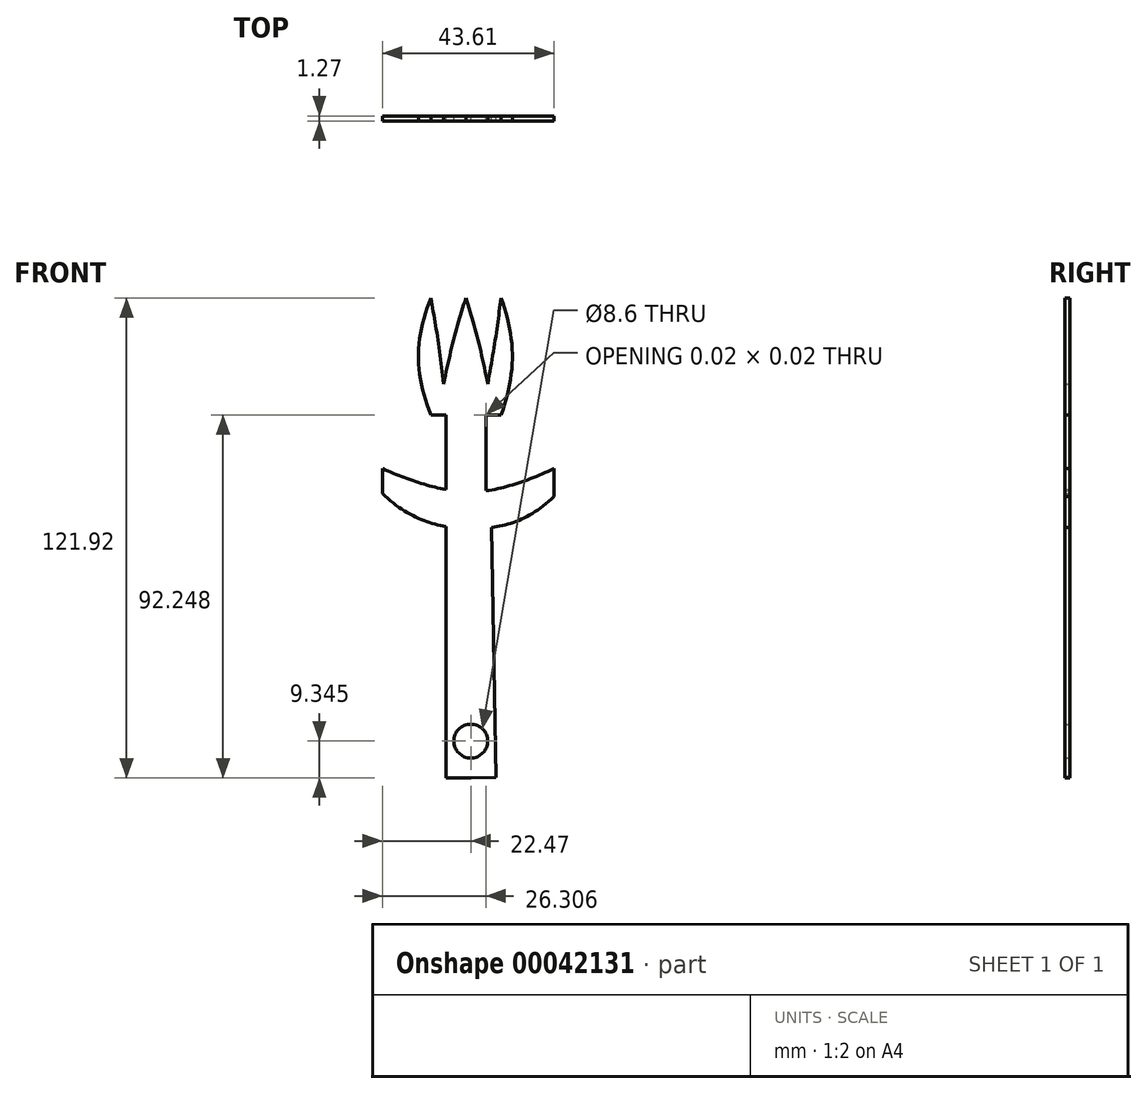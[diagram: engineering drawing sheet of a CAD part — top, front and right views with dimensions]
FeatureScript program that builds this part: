
annotation { "Feature Type Name" : "Feature", "Feature Type Description" : "" }
export const myFeature = defineFeature(function(context is Context, id is Id, definition is map)
    precondition{}
    {
        {
            var Q0;
            Q0=qCreatedBy(makeId("Front.planeOp"),FACE);
            var sketch = newSketch(context, id + "F0", { "sketchPlane" : qUnion([Q0])});
            skLineSegment(sketch, "E0", {"start": v(0, 0) * mm, "end": v(-6.35, 0) * mm});
            skLineSegment(sketch, "E1", {"start": v(0, 0) * mm, "end": v(6.35, 0.1) * mm});
            skFitSpline(sketch, "E2", {"points": [v(-22.47, 72.22) * mm, v(0, 63.3) * mm, v(21.14, 71.52) * mm], "startDerivative": vector(44.65, -42.56) * mm, "endDerivative": vector(42.56, 41.57) * mm});
            skLineSegment(sketch, "E3", {"start": v(-22.47, 72.22) * mm, "end": v(-22.47, 78.57) * mm});
            skLineSegment(sketch, "E4", {"start": v(21.14, 71.52) * mm, "end": v(21.14, 78.57) * mm});
            skFitSpline(sketch, "E5", {"points": [v(-22.47, 78.57) * mm, v(0, 72.7) * mm, v(21.14, 78.57) * mm], "startDerivative": vector(44.68, -19.03) * mm, "endDerivative": vector(42.53, 19.2) * mm});
            skPoint(sketch, "E6.end.orphan", {"position": v(17.01, 87.66) * mm});
            skPoint(sketch, "E7.start.orphan", {"position": v(12.12, 63.3) * mm});
            skPoint(sketch, "E8.start.orphan", {"position": v(-12.7, 63.3) * mm});
            skLineSegment(sketch, "E9", {"start": v(-6.35, 0) * mm, "end": v(-6.35, 63.83) * mm});
            skLineSegment(sketch, "E10", {"start": v(6.35, 0.1) * mm, "end": v(5.27, 63.6) * mm});
            skPoint(sketch, "E11.end.orphan", {"position": v(-6.75, 87.66) * mm});
            skLineSegment(sketch, "E12", {"start": v(-6.35, 92.26) * mm, "end": v(-6.35, 73.27) * mm});
            skPoint(sketch, "E13.orphan", {"position": v(0, 100.12) * mm});
            skPoint(sketch, "E14.orphan", {"position": v(5.27, 121.92) * mm});
            skPoint(sketch, "E15.1.internal.orphan", {"position": v(0, 137.97) * mm});
            skPoint(sketch, "E15.endDerivative.orphan", {"position": v(5.27, 97.92) * mm});
            skPoint(sketch, "E15.startDerivative.orphan", {"position": v(0, 121.92) * mm});
            skLineSegment(sketch, "E16", {"start": v(3.84, 92.26) * mm, "end": v(3.83, 92.26) * mm});
            skLineSegment(sketch, "E17", {"start": v(3.83, 92.26) * mm, "end": v(3.83, 72.96) * mm});
            skPoint(sketch, "E18.orphan", {"position": v(0, 92.26) * mm});
            skCircle(sketch, "E19", {"center": v(0, 9.34) * mm, "radius": 4.3 * mm});
            skLineSegment(sketch, "E20", {"start": v(-6.35, 92.26) * mm, "end": v(-6.38, 92.26) * mm});
            skPoint(sketch, "E21.start.orphan", {"position": v(-6.35, 121.92) * mm});
            skEllipticalArc(sketch, "E22", {});
            skPoint(sketch, "E23.orphan", {"position": v(-1.28, 121.92) * mm});
            skPoint(sketch, "E24.start.orphan", {"position": v(-1.26, 92.26) * mm});
            skPoint(sketch, "E25.orphan", {"position": v(7.65, 92.26) * mm});
            skLineSegment(sketch, "E26", {"start": v(-6.35, 92.22) * mm, "end": v(3.84, 92.22) * mm});
            skEllipticalArc(sketch, "E27.trimOffspring", {});
            skLineSegment(sketch, "E28", {"start": v(3.84, 92.22) * mm, "end": v(7.65, 92.22) * mm});
            skLineSegment(sketch, "E29", {"start": v(-6.35, 92.22) * mm, "end": v(-10.16, 92.22) * mm});
            skFitSpline(sketch, "E30", {"points": [v(-10.16, 92.22) * mm, v(-13.31, 107.1) * mm, v(-10.16, 121.92) * mm], "startDerivative": vector(-11.42, 29.74) * mm, "endDerivative": vector(11.43, 29.67) * mm});
            skPoint(sketch, "E31.1.internal.orphan", {"position": v(10.56, 107.1) * mm});
            skPoint(sketch, "E31.end.orphan", {"position": v(7.65, 121.92) * mm});
            skFitSpline(sketch, "E32", {"points": [v(7.65, 92.22) * mm, v(10.56, 107.1) * mm, v(7.65, 121.92) * mm], "startDerivative": vector(11.3, 29.74) * mm, "endDerivative": vector(-11.3, 29.67) * mm});
            skLineSegment(sketch, "E33", {"start": v(-6.9, 121.92) * mm, "end": v(-6.9, 121.92) * mm});
            skPoint(sketch, "E34.1.internal.orphan", {"position": v(-10.16, 112.43) * mm});
            skPoint(sketch, "E35.start.orphan", {"position": v(-6.9, 100.12) * mm});
            skPoint(sketch, "E36.1.internal.orphan", {"position": v(-6.9, 112.43) * mm});
            skPoint(sketch, "E37.1.internal.orphan", {"position": v(-4.08, 112.43) * mm});
            skPoint(sketch, "E38.start.orphan", {"position": v(5.27, 100.12) * mm});
            skPoint(sketch, "E39.end.orphan", {"position": v(-1.26, 121.92) * mm});
            skFitSpline(sketch, "E40", {"points": [v(-10.16, 121.92) * mm, v(-8.52, 112.43) * mm, v(-6.9, 100.12) * mm], "startDerivative": vector(3.6, -19.6) * mm, "endDerivative": vector(2.91, -23.92) * mm});
            skFitSpline(sketch, "E41", {"points": [v(-6.9, 100.12) * mm, v(-4.08, 112.43) * mm, v(-1.26, 121.92) * mm], "startDerivative": vector(5.15, 24) * mm, "endDerivative": vector(6.16, 19.51) * mm});
            skFitSpline(sketch, "E42", {"points": [v(-1.26, 121.92) * mm, v(1.57, 112.43) * mm, v(4.32, 100.12) * mm], "startDerivative": vector(6.22, -19.5) * mm, "endDerivative": vector(4.97, -24.02) * mm});
            skFitSpline(sketch, "E43", {"points": [v(7.65, 121.92) * mm, v(6.38, 112.43) * mm, v(4.32, 100.12) * mm], "startDerivative": vector(-2.45, -19.69) * mm, "endDerivative": vector(-4.18, -23.83) * mm});
            skPoint(sketch, "E44.end.orphan", {"position": v(-1.25, 92.22) * mm});
            skPoint(sketch, "E45.end.orphan", {"position": v(-12.55, 100.12) * mm});
            skPoint(sketch, "E46.start.orphan", {"position": v(-1.26, 100.12) * mm});
            skPoint(sketch, "E47.orphan", {"position": v(9.9, 100.12) * mm});
            const initialGuessF0  = {"E22": [-0.00127, 0.10709014901935063, 0, -1, 0.017645876799215893, 0.009439947865050294, 5.710609058103408, 5.714958242728358], "E27.trimOffspring": [-0.00127, 0.10709014901935063, 0, -1, 0.017645876799215893, 0.009439947865050294, 0.568227064451229, 0.572576249076178]};
            skSetInitialGuess(sketch, initialGuessF0);
            skSolve(sketch);
        }
        {
            var Q0;
            Q0=qSketchRegion(id+"F0",true);
            extrude(context, id + "F1", {"entities" : qUnion([Q0]), "depth" : 1.27 * mm});
        }
    });
